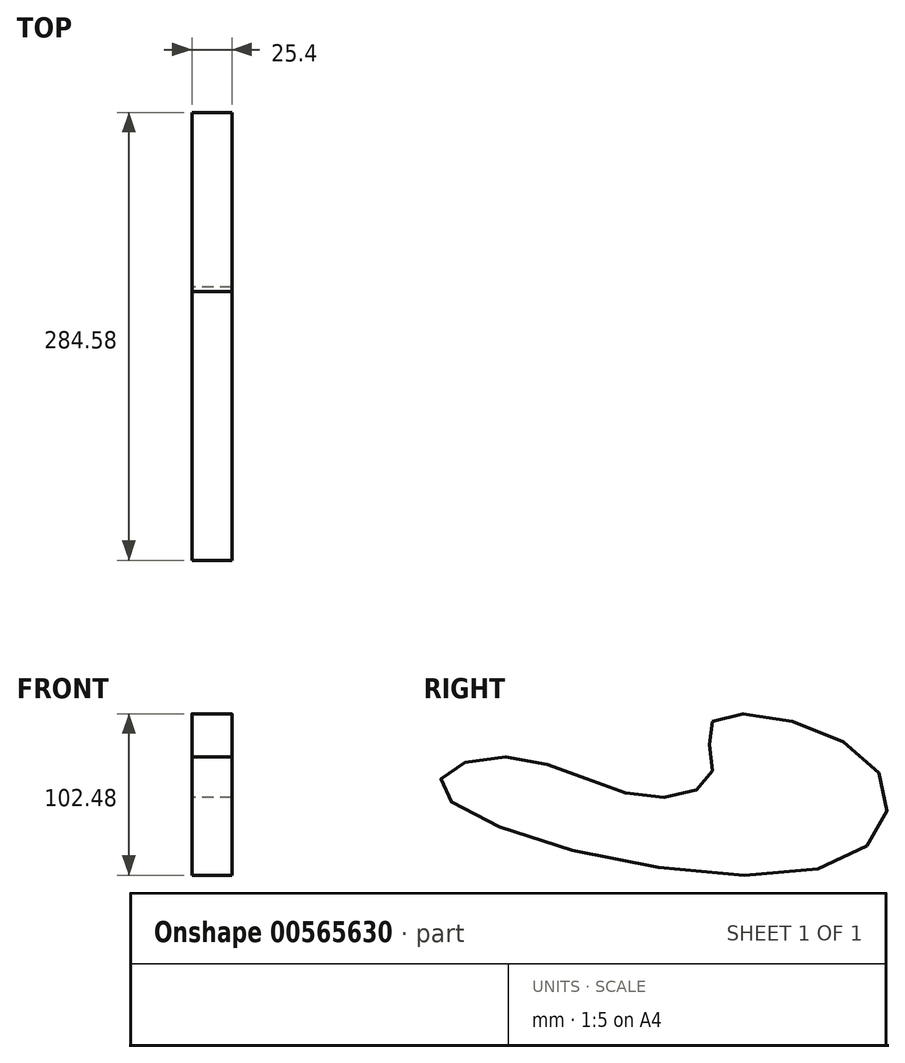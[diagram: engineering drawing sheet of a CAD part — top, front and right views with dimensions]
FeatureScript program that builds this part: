
annotation { "Feature Type Name" : "Feature", "Feature Type Description" : "" }
export const myFeature = defineFeature(function(context is Context, id is Id, definition is map)
    precondition{}
    {
        {
            var Q0;
            Q0=qCreatedBy(makeId("Right.planeOp"),FACE);
            var sketch = newSketch(context, id + "F0", { "sketchPlane" : qUnion([Q0])});
            skFitSpline(sketch, "E0", {"points": [v(0, 0) * mm, v(0, -32.04) * mm, v(-43.4, -47.54) * mm, v(-131.42, -22.29) * mm, v(-172.56, -43.12) * mm, v(77.66, -90.55) * mm, v(100.99, -26.4) * mm, v(0, 0) * mm]});
            skSolve(sketch);
        }
        {
            var Q0;
            Q0 = qSketchRegion(id + "F0", true);
            extrude(context, id + "F1", {"entities" : qUnion([Q0]), "depth" : 25.4 * mm, "offsetDistance" : 25.4 * mm});
        }
    });
